# Revit family: 4068738 Sylvania Lighting Fixture RAY RECTANGLE1 12LM BLADE LED 3K AL
name_source: partatom
category: Lighting Fixtures
revit_build: Autodesk Revit 2016 (Build: 20150220_1215(x64)
units: mm (PartAtom-declared; Revit-internal decimal feet)

## family parameters
Cut with Voids When Loaded = No
Host = Face
Light Source = Yes
OmniClass Number = 23.80.70.00
OmniClass Title = Lighting
Part Type = Normal
Room Calculation Point = No
Round Connector Dimension = Use Diameter
Shared = No

## types (1)
- 4068738 RAY/RECT1 12LM BLADE LED 3K AL
    Apparent Load = 4 VA
    Assembly Code = D5020200
    AssetType = Fixed
    Color Filter = 16777215
    Cost = 0 $
    Default Elevation = 1219 mm
    Description = Rectangular recessed wall luminairedie-cast aluminum, 112lm, 4W, 3lm/W, 3000K, CRI80+, asymmetric, non dimmable, IP65, IK08, (HxWxD) 190x190x65mm, 3 step MacAdam ellipse, Class II, 220-240V, A++ A+ A
    Dimming Lamp Color Temperature Shift = <None>
    DocumentationLiterature = http://www.sylvania-lighting.com
    DurationUnit = hours
    ElectricShockClassification = Class II
    Emit Shape Visible in Rendering = No
    Emit from Rectangle Length = 141 mm
    Emit from Rectangle Width = 6 mm  [stored 0.019685 ft]
    ExpectedLife = 50000
    Height_SYL = 190 mm  [stored 0.62336 ft]
    IfcExportAs = IfcLightFixtureType
    IfcExportType = IfcLightFixtureType
    ImpactProtectionIndex = IK08
    IngressProtection = IP65
    Keynote = 16500
    Lamp = LED
    LampColourRenderingIndex = 80
    LampColourTemperature = 3000 K
    LampNominalLuminous = 12 lm
    LampsType = LED
    LightOutputRatio = 100
    LightSourceYOffset_SYL = 0 mm  [stored 0 ft]
    LuminousEfficacy = 3 lm/W
    Manufacturer = Feilo Sylvania
    ManufacturerName = Feilo Sylvania
    Material = die-cast aluminum housing, safety tempered glass diffuser
    Material_1_SYL = Aluminum 7175 T73 0 Hot Formed
    Material_2_SYL = LED-Sylvania
    Material_3_SYL = <By Category>
    Material_4_SYL = <By Category>
    Model = RAY/RECTANGLE1 12LM BLADE LED 3K AL
    ModelNumber = 4068738
    ModelReference = RAY/RECTANGLE1 12LM BLADE LED 3K AL
    Name = RAY/RECTANGLE1 12LM BLADE LED 3K AL
    NominalHeight = 65 mm  [stored 0.213255 ft]
    NominalLength = 190 mm  [stored 0.62336 ft]
    NominalWidth = 0 mm  [stored 0 ft]
    Photometric Web File = 4068738.ies
    PowerConsumption = 4 W
    PowerFactor = 0
    RecessDepth_SYL = 65 mm  [stored 0.213255 ft]
    SlotHeight_SYL = 141 mm
    SlotStartHeight_SYL = 25 mm  [stored 0.082021 ft]
    SlotWidth_SYL = 6 mm  [stored 0.019685 ft]
    Square_SYL = No
    Tilt Angle = -90.00°
    Type Image = <None>
    TypeName = RAY/RECTANGLE1 12LM BLADE LED 3K AL
    URL = http://www.sylvania-lighting.com
    Voltage = 0 V
    Weight = 0.8 kg
    Width_SYL = 85 mm  [stored 0.278871 ft]

note: [stored X ft] marks values corroborated as IEEE doubles in the binary element streams (Revit-internal decimal feet)

## geometry (parser evidence)
native form markers: Sweep x3
no freeform markers — native parametric forms only
